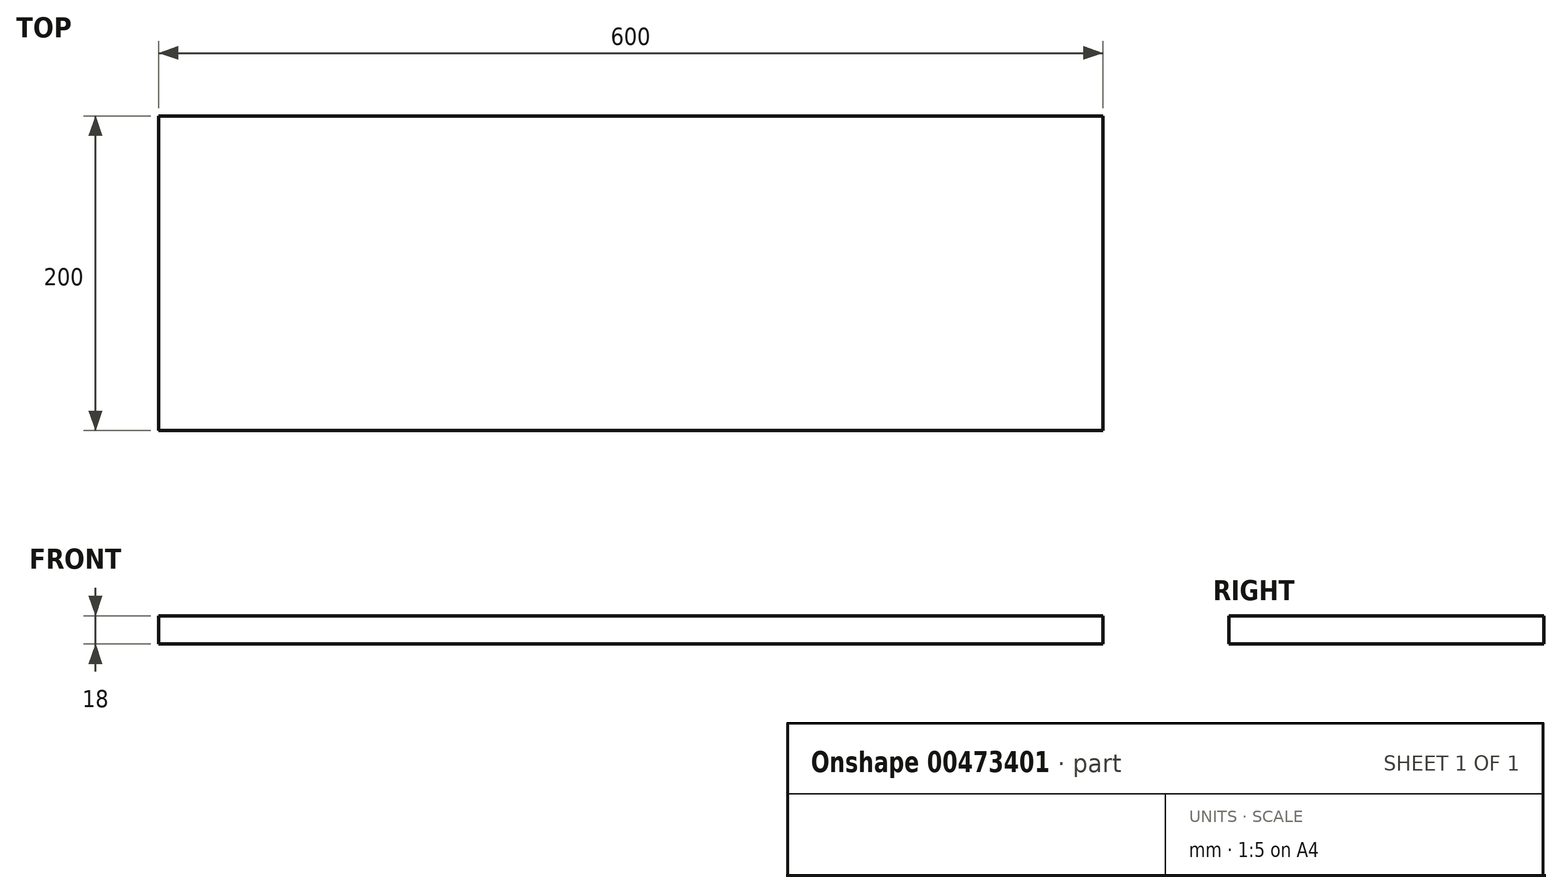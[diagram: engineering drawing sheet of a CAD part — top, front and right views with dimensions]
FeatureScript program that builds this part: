
annotation { "Feature Type Name" : "Feature", "Feature Type Description" : "" }
export const myFeature = defineFeature(function(context is Context, id is Id, definition is map)
    precondition{}
    {
        {
            var Q0;
            Q0=qCreatedBy(makeId("Top.planeOp"),FACE);
            var sketch = newSketch(context, id + "F0", { "sketchPlane" : qUnion([Q0])});
            skLineSegment(sketch, "E0.bottom", {"start": v(0, 0) * mm, "end": v(600, 0) * mm});
            skLineSegment(sketch, "E0.top", {"start": v(0, 200) * mm, "end": v(600, 200) * mm});
            skLineSegment(sketch, "E0.left", {"start": v(0, 0) * mm, "end": v(0, 200) * mm});
            skLineSegment(sketch, "E0.right", {"start": v(600, 0) * mm, "end": v(600, 200) * mm});
            skSolve(sketch);
        }
        {
            var Q0;
            Q0 = qSketchRegion(id + "F0", true);
            extrude(context, id + "F1", {"entities" : qUnion([Q0]), "depth" : 18 * mm});
        }
    });
